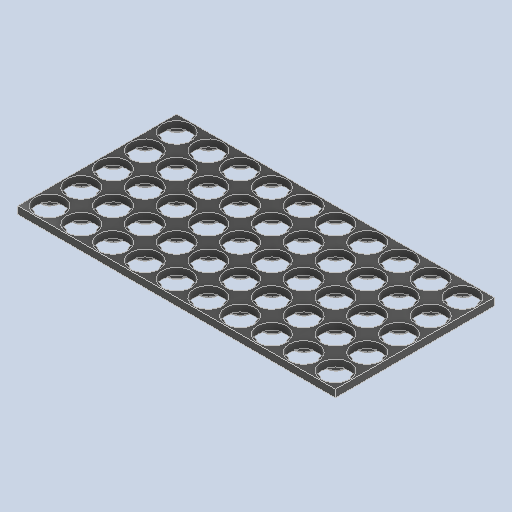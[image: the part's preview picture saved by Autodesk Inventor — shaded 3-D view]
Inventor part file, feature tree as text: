
AUTODESK INVENTOR PART (.ipt)
format: ipt  version: 2023 (Build 270158000, 158)  size: 510,464 bytes
history: native  units: in
note: dims shown in document units (in); Inventor stores cm internally (conversion verified against a paired STEP export)
features: extrude x2, sketch x1, pattern_linear x1
ambient origin geometry x8: Origin, YZ Plane, XZ Plane, XY Plane, X Axis, Y Axis, Z Axis, Center Point
bodies: Solid1 (feature_tree)
feature tree (4):
  sketch  "Sketch1"  dims[d0=0.8268in d1=0.9055in d2=0.1969in d3=0.0in d4=1.5748in d6=360.0deg d8=0.0197in d9=0.0in d10=3.937in d12=0.9055in d13=1.9685in d15=0.9055in]
  extrude  "Extrusion1"  Depth=0.9055in
  extrude  "Extrusion2"  Depth=0.1969in TaperAngle=0.0deg
  pattern_linear  "Rectangular Pattern1"  Count1=4 Spacing1=360.0deg
